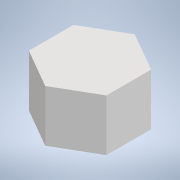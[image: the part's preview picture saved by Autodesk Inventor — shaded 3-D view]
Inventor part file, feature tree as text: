
AUTODESK INVENTOR PART (.ipt)
format: ipt  version: 2021 (Build 250183000, 183)  size: 105,472 bytes
history: native  units: mm
features: sketch x7, extrude x1
ambient origin geometry x8: Origin, YZ Plane, XZ Plane, XY Plane, X Axis, Y Axis, Z Axis, Center Point
bodies: Solid1 (feature_tree)
feature tree (8):
  extrude  "Extrusion1"  Depth=800.0mm TaperAngle=0.0deg
  sketch  "Sketch2"  dims[d3=400.0mm]
  sketch  "Sketch3"
  sketch  "Sketch4"
  sketch  "Sketch5"
  sketch  "Sketch6"
  sketch  "Sketch7"
  sketch  "Sketch1"  dims[d0=1200.0mm d1=800.0mm d2=0.0mm]
